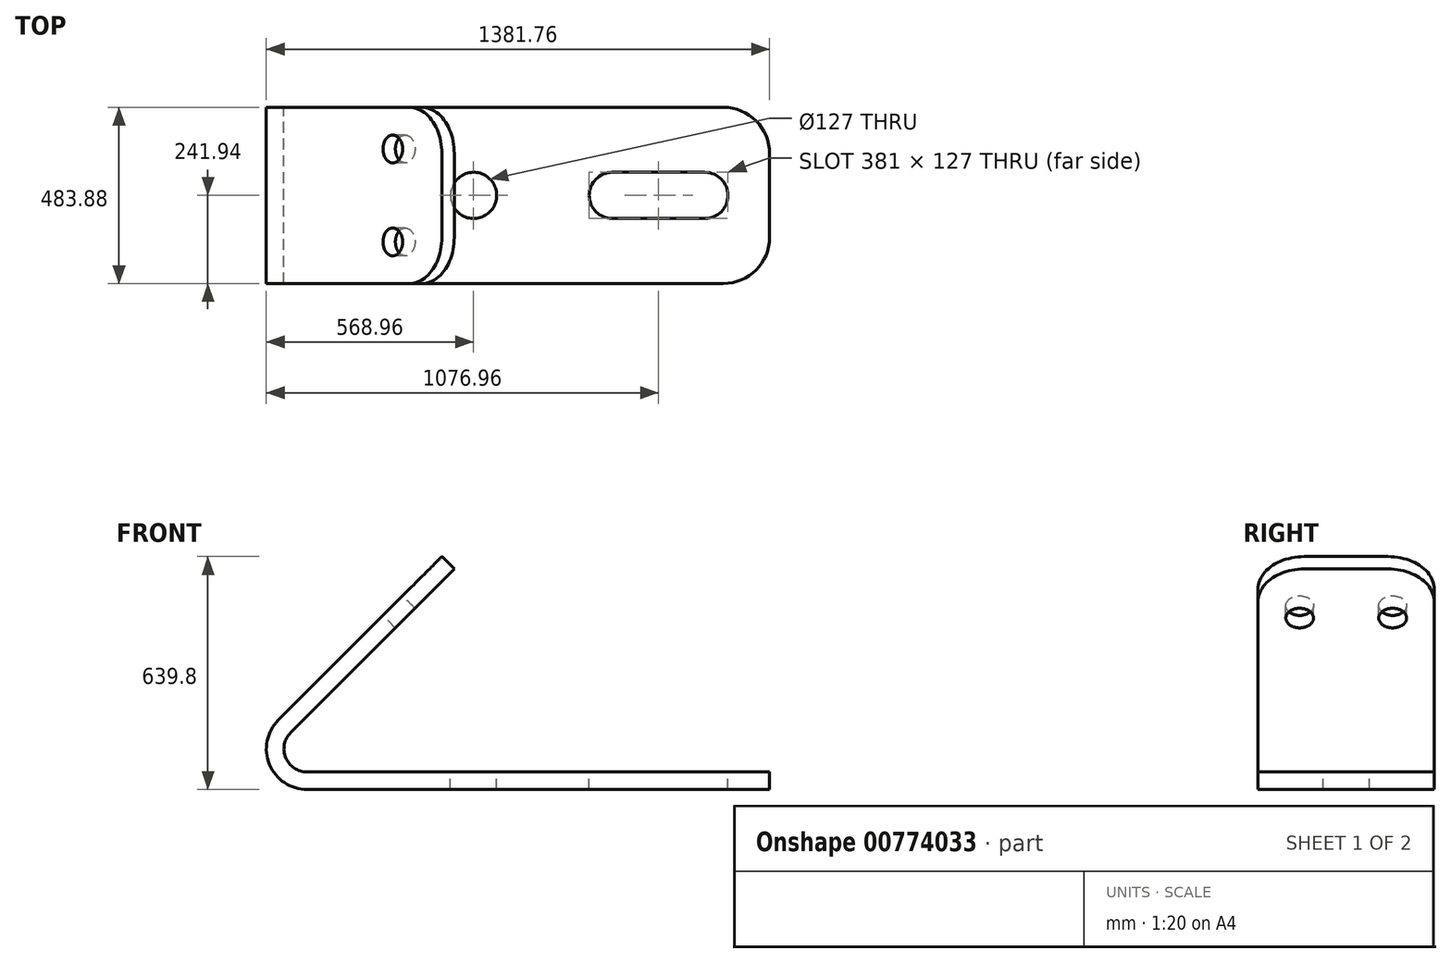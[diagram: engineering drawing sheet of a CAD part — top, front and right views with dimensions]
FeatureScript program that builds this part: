
annotation { "Feature Type Name" : "Feature", "Feature Type Description" : "" }
export const myFeature = defineFeature(function(context is Context, id is Id, definition is map)
    precondition{}
    {
        {
            var Q0;
            Q0=qCreatedBy(makeId("Front.planeOp"),FACE);
            var sketch = newSketch(context, id + "F0", { "sketchPlane" : qUnion([Q0])});
            skLineSegment(sketch, "E0.bottom", {"start": v(635, -24.13) * mm, "end": v(-635, -24.13) * mm});
            skLineSegment(sketch, "E0.top", {"start": v(635, 24.13) * mm, "end": v(-635, 24.13) * mm});
            skLineSegment(sketch, "E0.left", {"start": v(635, -24.13) * mm, "end": v(635, 24.13) * mm});
            skLineSegment(sketch, "E0.right", {"start": v(-635, -24.13) * mm, "end": v(-635, 24.13) * mm});
            skPoint(sketch, "E0.middle", {"position": v(0, 0) * mm});
            skArc(sketch, "E1", {"start": v(-714.03, 166.66) * mm, "mid": v(-738.25, 44.86) * mm, "end": v(-635, -24.13) * mm});
            skArc(sketch, "E2", {"start": v(-679.9, 132.53) * mm, "mid": v(-693.67, 63.33) * mm, "end": v(-635, 24.13) * mm});
            skLineSegment(sketch, "E3", {"start": v(-714.03, 166.66) * mm, "end": v(-634.89, 245.8) * mm});
            skLineSegment(sketch, "E4", {"start": v(-714.03, 166.66) * mm, "end": v(-635, 87.63) * mm, "construction": true});
            skLineSegment(sketch, "E5", {"start": v(-714.03, 166.66) * mm, "end": v(-265.01, 615.67) * mm});
            skLineSegment(sketch, "E6", {"start": v(-265.01, 615.67) * mm, "end": v(-230.89, 581.54) * mm});
            skLineSegment(sketch, "E7", {"start": v(-230.89, 581.54) * mm, "end": v(-679.9, 132.53) * mm});
            skSolve(sketch);
        }
        {
            var Q0;
            Q0=makeQuery(id+"F0.imprint","IMPRINT",FACE,{"disambiguationData":[TD([[makeQuery(id+"F0.imprint","IMPRINT",EDGE,{"derivedFrom":sQuery(id+"F0.wireOp",EDGE,"E0.right")}),1.0]])]});
            var Q1;
            Q1=makeQuery(id+"F0.imprint","IMPRINT",FACE,{"disambiguationData":[TD([[makeQuery(id+"F0.imprint","IMPRINT",EDGE,{"derivedFrom":sQuery(id+"F0.wireOp",EDGE,"E0.bottom")}),-1.0]])]});
            extrude(context, id + "F1", {"entities" : qUnion([Q0, Q1]), "depth" : 241.94 * mm, "offsetDistance" : 25.4 * mm, "hasSecondDirection" : true, "secondDirectionOppositeDirection" : true, "secondDirectionDepth" : 241.94 * mm});
        }
        {
            var Q0;
            Q0=makeQuery(id+"F1.opExtrude","CAP_EDGE",EDGE,{"disambiguationData":[OSD([sQuery(id+"F0.wireOp",EDGE,"E6")])],"isStart":false});
            var Q1;
            Q1=makeQuery(id+"F1.opExtrude","CAP_EDGE",EDGE,{"disambiguationData":[OSD([sQuery(id+"F0.wireOp",EDGE,"E6")])],"isStart":true});
            var Q2;
            Q2=makeQuery(id+"F1.opExtrude","CAP_EDGE",EDGE,{"disambiguationData":[OSD([sQuery(id+"F0.wireOp",EDGE,"E0.left")])],"isStart":true});
            var Q3;
            Q3=makeQuery(id+"F1.opExtrude","CAP_EDGE",EDGE,{"disambiguationData":[OSD([sQuery(id+"F0.wireOp",EDGE,"E0.left")])],"isStart":false});
            fillet(context, id + "F2", {"entities" : qUnion([Q0, Q1, Q2, Q3]), "radius" : 127 * mm, "tangentPropagation" : true, "allowEdgeOverflow" : false});
        }
        {
            var Q0;
            Q0=makeQuery(id+"F1.opExtrude","SWEPT_FACE",FACE,{"disambiguationData":[OSD([sQuery(id+"F0.wireOp",EDGE,"E5")])]});
            var sketch = newSketch(context, id + "F3", { "sketchPlane" : qUnion([Q0])});
            skLineSegment(sketch, "E8", {"start": v(-241.94, 69.16) * mm, "end": v(-127.64, 69.16) * mm, "construction": true});
            skLineSegment(sketch, "E9", {"start": v(-127.64, 247.95) * mm, "end": v(-127.64, 57.45) * mm, "construction": true});
            skCircle(sketch, "E10", {"center": v(-127.64, 57.45) * mm, "radius": 38.1 * mm});
            skLineSegment(sketch, "E11", {"start": v(-127.64, 57.45) * mm, "end": v(127.64, 57.45) * mm, "construction": true});
            skCircle(sketch, "E12", {"center": v(127.64, 57.45) * mm, "radius": 38.1 * mm});
            skSolve(sketch);
        }
        {
            var Q0;
            Q0 = qSketchRegion(id + "F3", true);
            extrude(context, id + "F4", {"entities" : qUnion([Q0]), "operationType" : NewBodyOperationType.REMOVE, "oppositeDirection" : true, "depth" : 127 * mm, "offsetDistance" : 25.4 * mm});
        }
        {
            var Q0;
            Q0 = qSketchRegion(id + "F3", true);
            extrude(context, id + "F5", {"entities" : qUnion([Q0]), "operationType" : NewBodyOperationType.REMOVE, "oppositeDirection" : true, "depth" : 127 * mm, "offsetDistance" : 25.4 * mm});
        }
        {
            var Q0;
            Q0=makeQuery(id+"F1.opExtrude","SWEPT_FACE",FACE,{"disambiguationData":[OSD([sQuery(id+"F0.wireOp",EDGE,"E0.top")])]});
            var sketch = newSketch(context, id + "F6", { "sketchPlane" : qUnion([Q0])});
            skLineSegment(sketch, "E13", {"start": v(635, 0) * mm, "end": v(520.7, 0) * mm, "construction": true});
            skPoint(sketch, "E13.endSnap0", {"position": v(635, 0) * mm});
            skCircle(sketch, "E14", {"center": v(-177.8, 0) * mm, "radius": 63.5 * mm});
            skLineSegment(sketch, "E15", {"start": v(520.7, 0) * mm, "end": v(457.2, 0) * mm, "construction": true});
            skArc(sketch, "E16", {"start": v(457.2, -63.5) * mm, "mid": v(520.7, 0) * mm, "end": v(457.2, 63.5) * mm});
            skArc(sketch, "E17", {"start": v(203.2, 63.5) * mm, "mid": v(139.7, 0) * mm, "end": v(203.2, -63.5) * mm});
            skLineSegment(sketch, "E18", {"start": v(203.2, -63.5) * mm, "end": v(457.2, -63.5) * mm});
            skLineSegment(sketch, "E19", {"start": v(203.2, 63.5) * mm, "end": v(457.2, 63.5) * mm});
            skLineSegment(sketch, "E20.trimOffspring", {"start": v(139.7, 0) * mm, "end": v(-177.8, 0) * mm, "construction": true});
            skSolve(sketch);
        }
        {
            var Q0;
            Q0=makeQuery(id+"F6.imprint","IMPRINT",FACE,{"disambiguationData":[TD([[makeQuery(id+"F6.imprint","IMPRINT",EDGE,{"derivedFrom":sQuery(id+"F6.wireOp",EDGE,"E14")}),1.0]])]});
            var Q1;
            Q1=makeQuery(id+"F6.imprint","IMPRINT",FACE,{"disambiguationData":[TD([[makeQuery(id+"F6.imprint","IMPRINT",EDGE,{"derivedFrom":sQuery(id+"F6.wireOp",EDGE,"E16")}),1.0]])]});
            extrude(context, id + "F7", {"entities" : qUnion([Q0, Q1]), "operationType" : NewBodyOperationType.REMOVE, "oppositeDirection" : true, "depth" : 127 * mm, "offsetDistance" : 25.4 * mm});
        }
    });
